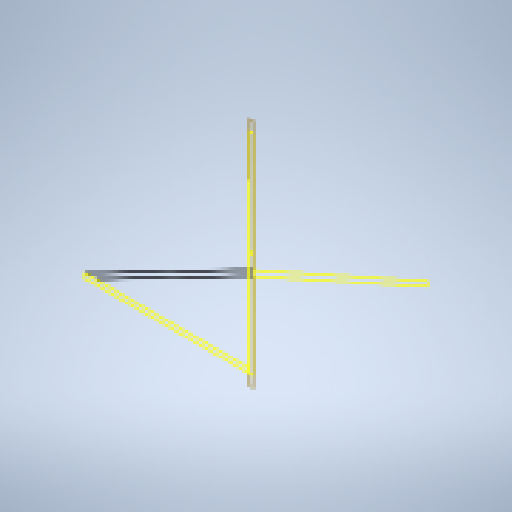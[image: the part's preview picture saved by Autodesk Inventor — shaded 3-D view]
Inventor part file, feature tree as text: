
AUTODESK INVENTOR PART (.ipt)
format: ipt  version: 2025 (Build 290162000, 162)  size: 131,072 bytes
history: native  units: in
note: dims shown in document units (in); Inventor stores cm internally (conversion verified against a paired STEP export)
features: other x5, reference x3, plane x1, sketch x1
ambient origin geometry x8: Origin, YZ Plane, XZ Plane, XY Plane, X Axis, Y Axis, Z Axis, Center Point
feature tree (10):
  plane  "Work Plane1"
  sketch  "Sketch1"
  reference  "Reference1"
  reference  "Reference2"
  reference  "Reference3"
  other  "<userpath>\Documents\GitHub\USCTigerBurn24\v2\Tiger.iam"
  other  "Tiger.iam"
  other  "2x4x72:15"
  other  "2X4X92:1"
  other  "back slant:4"
